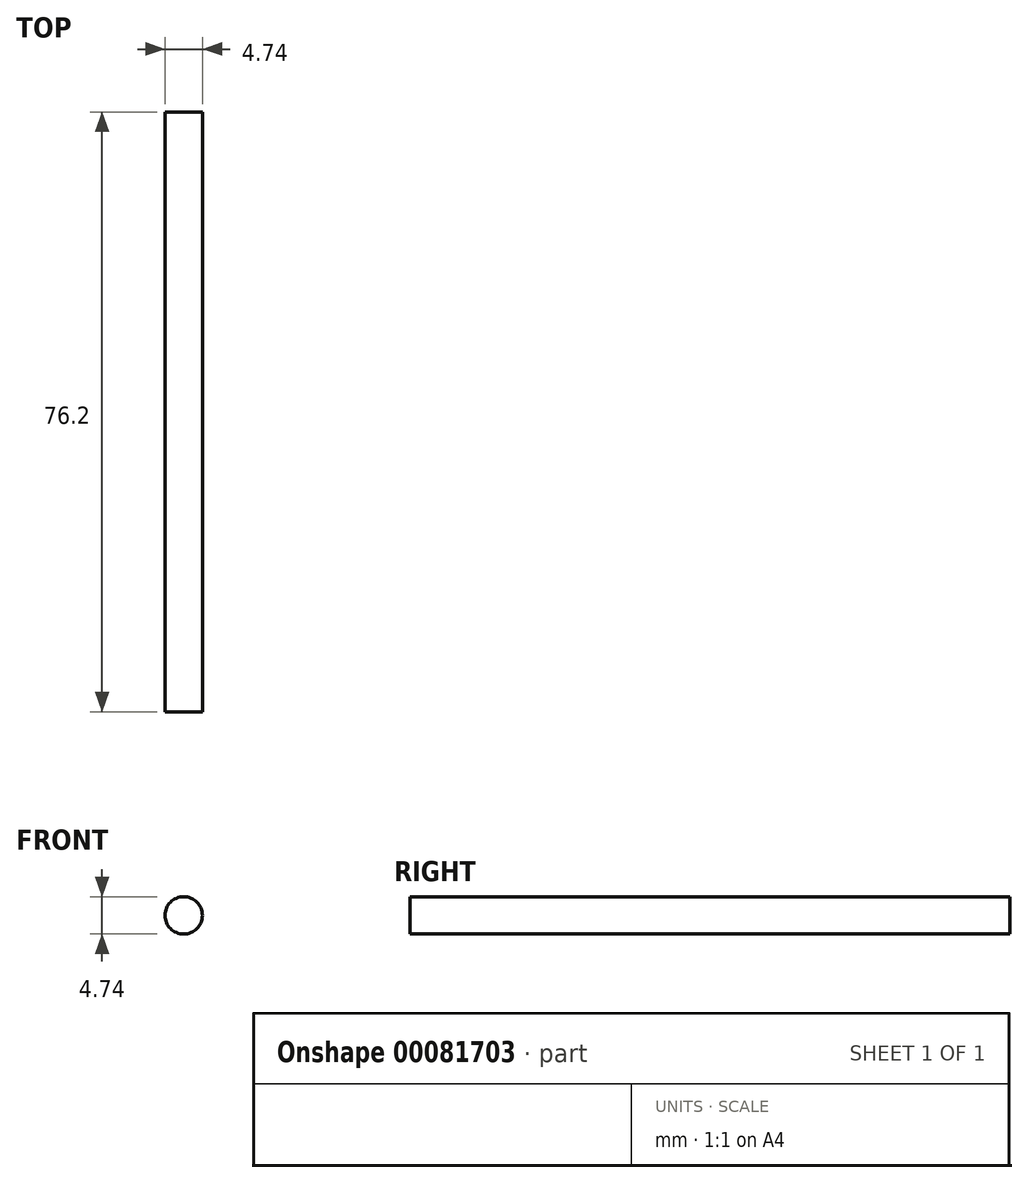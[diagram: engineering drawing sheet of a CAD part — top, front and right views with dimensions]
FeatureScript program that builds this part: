
annotation { "Feature Type Name" : "Feature", "Feature Type Description" : "" }
export const myFeature = defineFeature(function(context is Context, id is Id, definition is map)
    precondition{}
    {
        {
            var Q0;
            Q0=qCreatedBy(makeId("Front.planeOp"),FACE);
            var sketch = newSketch(context, id + "F0", { "sketchPlane" : qUnion([Q0])});
            skCircle(sketch, "E0", {"center": v(0, 0) * mm, "radius": 2.37 * mm});
            skSolve(sketch);
        }
        {
            var Q0;
            Q0 = qSketchRegion(id + "F0", true);
            extrude(context, id + "F1", {"entities" : qUnion([Q0]), "depth" : 76.2 * mm});
        }
    });
